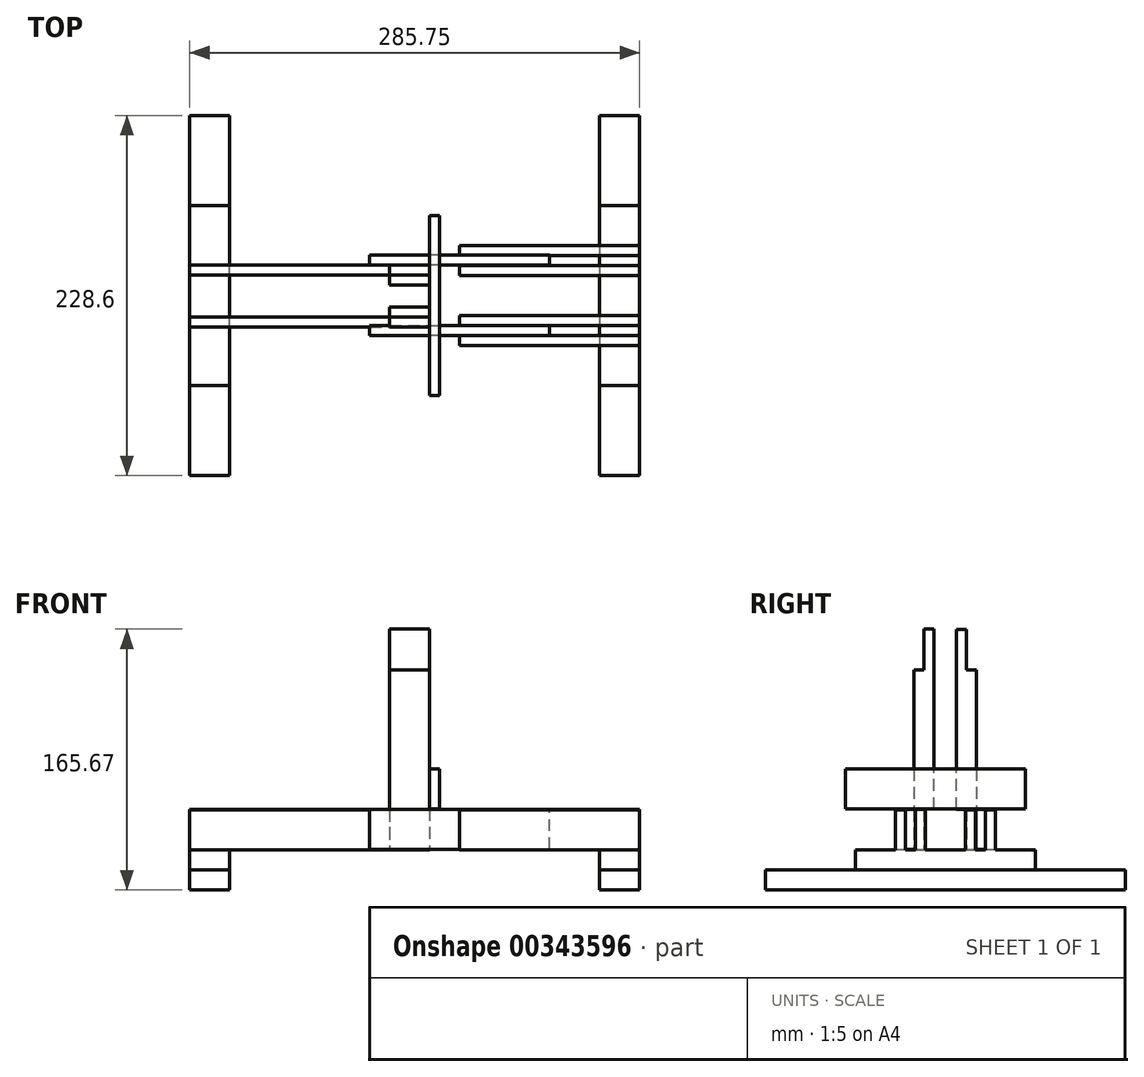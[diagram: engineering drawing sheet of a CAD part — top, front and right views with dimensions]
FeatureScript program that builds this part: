
annotation { "Feature Type Name" : "Feature", "Feature Type Description" : "" }
export const myFeature = defineFeature(function(context is Context, id is Id, definition is map)
    precondition{}
    {
        {
            var Q0;
            Q0=qCreatedBy(makeId("Top.planeOp"),FACE);
            var sketch = newSketch(context, id + "F0", { "sketchPlane" : qUnion([Q0])});
            skLineSegment(sketch, "E0.bottom", {"start": v(0, 0) * mm, "end": v(25.4, 0) * mm});
            skLineSegment(sketch, "E0.top", {"start": v(0, 114.3) * mm, "end": v(25.4, 114.3) * mm});
            skLineSegment(sketch, "E0.left", {"start": v(0, 0) * mm, "end": v(0, 114.3) * mm});
            skLineSegment(sketch, "E0.right", {"start": v(25.4, 0) * mm, "end": v(25.4, 114.3) * mm});
            skLineSegment(sketch, "E1.bottom", {"start": v(-234.95, 0) * mm, "end": v(-260.35, 0) * mm});
            skLineSegment(sketch, "E1.top", {"start": v(-234.95, 114.3) * mm, "end": v(-260.35, 114.3) * mm});
            skLineSegment(sketch, "E1.left", {"start": v(-234.95, 0) * mm, "end": v(-234.95, 114.3) * mm});
            skLineSegment(sketch, "E1.right", {"start": v(-260.35, 0) * mm, "end": v(-260.35, 114.3) * mm});
            skLineSegment(sketch, "E2.bottom", {"start": v(-260.35, 114.3) * mm, "end": v(-234.95, 114.3) * mm});
            skLineSegment(sketch, "E2.top", {"start": v(-260.35, 228.6) * mm, "end": v(-234.95, 228.6) * mm});
            skLineSegment(sketch, "E2.left", {"start": v(-260.35, 114.3) * mm, "end": v(-260.35, 228.6) * mm});
            skLineSegment(sketch, "E2.right", {"start": v(-234.95, 114.3) * mm, "end": v(-234.95, 228.6) * mm});
            skLineSegment(sketch, "E3.top", {"start": v(0, 228.6) * mm, "end": v(25.4, 228.6) * mm});
            skLineSegment(sketch, "E3.left", {"start": v(0, 114.3) * mm, "end": v(0, 228.6) * mm});
            skLineSegment(sketch, "E3.right", {"start": v(25.4, 114.3) * mm, "end": v(25.4, 228.6) * mm});
            skSolve(sketch);
        }
        {
            var Q0;
            Q0 = qSketchRegion(id + "F0", true);
            extrude(context, id + "F1", {"entities" : qUnion([Q0]), "depth" : 12.7 * mm});
        }
        {
            var Q0;
            Q0=makeQuery(id+"F1.opExtrude","CAP_FACE",FACE,{"disambiguationData":[OSD([sQuery(id+"F0.wireOp",EDGE,"E1.bottom"),sQuery(id+"F0.wireOp",EDGE,"E1.left"),sQuery(id+"F0.wireOp",EDGE,"E1.right"),sQuery(id+"F0.wireOp",EDGE,"E2.top"),sQuery(id+"F0.wireOp",EDGE,"E2.left"),sQuery(id+"F0.wireOp",EDGE,"E2.right")])],"isStart":false});
            var sketch = newSketch(context, id + "F2", { "sketchPlane" : qUnion([Q0])});
            skLineSegment(sketch, "E4.bottom", {"start": v(-260.35, 57.15) * mm, "end": v(-234.95, 57.15) * mm});
            skLineSegment(sketch, "E4.top", {"start": v(-260.35, 171.45) * mm, "end": v(-234.95, 171.45) * mm});
            skLineSegment(sketch, "E4.left", {"start": v(-260.35, 57.15) * mm, "end": v(-260.35, 171.45) * mm});
            skLineSegment(sketch, "E4.right", {"start": v(-234.95, 57.15) * mm, "end": v(-234.95, 171.45) * mm});
            skLineSegment(sketch, "E5.bottom", {"start": v(0, 171.45) * mm, "end": v(25.4, 171.45) * mm});
            skLineSegment(sketch, "E5.top", {"start": v(0, 57.15) * mm, "end": v(25.4, 57.15) * mm});
            skLineSegment(sketch, "E5.left", {"start": v(0, 171.45) * mm, "end": v(0, 57.15) * mm});
            skLineSegment(sketch, "E5.right", {"start": v(25.4, 171.45) * mm, "end": v(25.4, 57.15) * mm});
            skSolve(sketch);
        }
        {
            var Q0;
            Q0 = qSketchRegion(id + "F2", true);
            extrude(context, id + "F3", {"entities" : qUnion([Q0]), "depth" : 12.7 * mm});
        }
        {
            var Q0;
            Q0=makeQuery(id+"F3.opExtrude","SWEPT_FACE",FACE,{"disambiguationData":[OSD([sQuery(id+"F2.wireOp",EDGE,"E5.right")])]});
            var sketch = newSketch(context, id + "F4", { "sketchPlane" : qUnion([Q0])});
            skLineSegment(sketch, "E6.bottom", {"start": v(82.55, 25.4) * mm, "end": v(88.9, 25.4) * mm});
            skLineSegment(sketch, "E6.top", {"start": v(82.55, 50.8) * mm, "end": v(88.9, 50.8) * mm});
            skLineSegment(sketch, "E6.left", {"start": v(82.55, 25.4) * mm, "end": v(82.55, 50.8) * mm});
            skLineSegment(sketch, "E6.right", {"start": v(88.9, 25.4) * mm, "end": v(88.9, 50.8) * mm});
            skLineSegment(sketch, "E7.bottom", {"start": v(139.7, 25.4) * mm, "end": v(146.05, 25.4) * mm});
            skLineSegment(sketch, "E7.top", {"start": v(139.7, 50.8) * mm, "end": v(146.05, 50.8) * mm});
            skLineSegment(sketch, "E7.left", {"start": v(139.7, 25.4) * mm, "end": v(139.7, 50.8) * mm});
            skLineSegment(sketch, "E7.right", {"start": v(146.05, 25.4) * mm, "end": v(146.05, 50.8) * mm});
            skLineSegment(sketch, "E8.bottom", {"start": v(95.25, 25.4) * mm, "end": v(101.6, 25.4) * mm});
            skLineSegment(sketch, "E8.top", {"start": v(95.25, 51.24) * mm, "end": v(101.6, 51.24) * mm});
            skLineSegment(sketch, "E8.left", {"start": v(95.25, 25.4) * mm, "end": v(95.25, 51.24) * mm});
            skLineSegment(sketch, "E8.right", {"start": v(101.6, 25.4) * mm, "end": v(101.6, 51.24) * mm});
            skLineSegment(sketch, "E9.bottom", {"start": v(127, 25.4) * mm, "end": v(133.35, 25.4) * mm});
            skLineSegment(sketch, "E9.top", {"start": v(127, 50.9) * mm, "end": v(133.35, 50.9) * mm});
            skLineSegment(sketch, "E9.left", {"start": v(127, 25.4) * mm, "end": v(127, 50.9) * mm});
            skLineSegment(sketch, "E9.right", {"start": v(133.35, 25.4) * mm, "end": v(133.35, 50.9) * mm});
            skSolve(sketch);
        }
        {
            var Q0;
            Q0 = qSketchRegion(id + "F4", true);
            extrude(context, id + "F5", {"entities" : qUnion([Q0]), "operationType" : NewBodyOperationType.ADD, "oppositeDirection" : true, "depth" : 114.3 * mm});
        }
        {
            var Q0;
            Q0=makeQuery(id+"F5.opExtrude","SWEPT_FACE",FACE,{"disambiguationData":[OSD([sQuery(id+"F4.wireOp",EDGE,"E8.top")])]});
            var sketch = newSketch(context, id + "F6", { "sketchPlane" : qUnion([Q0])});
            skLineSegment(sketch, "E10.bottom", {"start": v(-31.75, 95.25) * mm, "end": v(-146.05, 95.25) * mm});
            skLineSegment(sketch, "E10.top", {"start": v(-31.75, 88.9) * mm, "end": v(-146.05, 88.9) * mm});
            skLineSegment(sketch, "E10.left", {"start": v(-31.75, 95.25) * mm, "end": v(-31.75, 88.9) * mm});
            skLineSegment(sketch, "E10.right", {"start": v(-146.05, 95.25) * mm, "end": v(-146.05, 88.9) * mm});
            skPoint(sketch, "E11.firstSnap0", {"position": v(-31.75, 101.6) * mm});
            skLineSegment(sketch, "E11.bottom", {"start": v(-31.75, 140.03) * mm, "end": v(-146.05, 140.03) * mm});
            skLineSegment(sketch, "E11.top", {"start": v(-31.75, 133.68) * mm, "end": v(-146.05, 133.68) * mm});
            skLineSegment(sketch, "E11.left", {"start": v(-31.75, 140.03) * mm, "end": v(-31.75, 133.68) * mm});
            skLineSegment(sketch, "E11.right", {"start": v(-146.05, 140.03) * mm, "end": v(-146.05, 133.68) * mm});
            skSolve(sketch);
        }
        {
            var Q0;
            Q0 = qSketchRegion(id + "F6", true);
            extrude(context, id + "F7", {"entities" : qUnion([Q0]), "oppositeDirection" : true, "depth" : 25.4 * mm});
        }
        {
            var Q0;
            Q0=makeQuery(id+"F7.opExtrude","SWEPT_FACE",FACE,{"disambiguationData":[OSD([sQuery(id+"F6.wireOp",EDGE,"E11.top")])]});
            var sketch = newSketch(context, id + "F8", { "sketchPlane" : qUnion([Q0])});
            skLineSegment(sketch, "E12.bottom", {"start": v(-133.35, 51.24) * mm, "end": v(-260.35, 51.24) * mm});
            skLineSegment(sketch, "E12.top", {"start": v(-133.35, 25.84) * mm, "end": v(-260.35, 25.84) * mm});
            skLineSegment(sketch, "E12.left", {"start": v(-133.35, 51.24) * mm, "end": v(-133.35, 25.84) * mm});
            skLineSegment(sketch, "E12.right", {"start": v(-260.35, 51.24) * mm, "end": v(-260.35, 25.84) * mm});
            skSolve(sketch);
        }
        {
            var Q0;
            Q0=makeQuery(id+"F8.imprint","IMPRINT",FACE,{"disambiguationData":[TD([[makeQuery(id+"F8.imprint","IMPRINT",EDGE,{"derivedFrom":sQuery(id+"F8.wireOp",EDGE,"E12.bottom")}),1.0]])]});
            extrude(context, id + "F9", {"entities" : qUnion([Q0]), "depth" : 6.35 * mm});
        }
        {
            var Q0;
            Q0=makeQuery(id+"F3.opExtrude","CAP_FACE",FACE,{"disambiguationData":[OSD([sQuery(id+"F2.wireOp",EDGE,"E4.bottom"),sQuery(id+"F2.wireOp",EDGE,"E4.top"),sQuery(id+"F2.wireOp",EDGE,"E4.left"),sQuery(id+"F2.wireOp",EDGE,"E4.right")])],"isStart":false});
            var sketch = newSketch(context, id + "F10", { "sketchPlane" : qUnion([Q0])});
            skLineSegment(sketch, "E13.bottom", {"start": v(-260.35, 94.23) * mm, "end": v(-133.35, 94.23) * mm});
            skLineSegment(sketch, "E13.top", {"start": v(-260.35, 100.58) * mm, "end": v(-133.35, 100.58) * mm});
            skLineSegment(sketch, "E13.left", {"start": v(-260.35, 94.23) * mm, "end": v(-260.35, 100.58) * mm});
            skLineSegment(sketch, "E13.right", {"start": v(-133.35, 94.23) * mm, "end": v(-133.35, 100.58) * mm});
            skSolve(sketch);
        }
        {
            var Q0;
            Q0 = qSketchRegion(id + "F10", true);
            extrude(context, id + "F11", {"entities" : qUnion([Q0]), "depth" : 25.4 * mm});
        }
        {
            var Q0;
            Q0=makeQuery(id+"F11.opExtrude","CAP_FACE",FACE,{"disambiguationData":[OSD([sQuery(id+"F10.wireOp",EDGE,"E13.bottom"),sQuery(id+"F10.wireOp",EDGE,"E13.top"),sQuery(id+"F10.wireOp",EDGE,"E13.left"),sQuery(id+"F10.wireOp",EDGE,"E13.right")])],"isStart":true});
            var sketch = newSketch(context, id + "F12", { "sketchPlane" : qUnion([Q0])});
            skPoint(sketch, "E14.left.start.orphan", {"position": v(-88.9, -133.2) * mm});
            skLineSegment(sketch, "E15.bottom", {"start": v(-133.35, -94.23) * mm, "end": v(-107.95, -94.23) * mm});
            skLineSegment(sketch, "E15.top", {"start": v(-133.35, -100.58) * mm, "end": v(-107.95, -100.58) * mm});
            skLineSegment(sketch, "E15.left", {"start": v(-133.35, -94.23) * mm, "end": v(-133.35, -100.58) * mm});
            skLineSegment(sketch, "E15.right", {"start": v(-107.95, -94.23) * mm, "end": v(-107.95, -100.58) * mm});
            skLineSegment(sketch, "E16.bottom", {"start": v(-133.35, -127.38) * mm, "end": v(-107.95, -127.38) * mm});
            skLineSegment(sketch, "E16.top", {"start": v(-133.35, -133.73) * mm, "end": v(-107.95, -133.73) * mm});
            skLineSegment(sketch, "E16.left", {"start": v(-133.35, -127.38) * mm, "end": v(-133.35, -133.73) * mm});
            skLineSegment(sketch, "E16.right", {"start": v(-107.95, -127.38) * mm, "end": v(-107.95, -133.73) * mm});
            skSolve(sketch);
        }
        {
            var Q0;
            Q0 = qSketchRegion(id + "F12", true);
            extrude(context, id + "F13", {"entities" : qUnion([Q0]), "oppositeDirection" : true, "depth" : 114.3 * mm});
        }
        {
            var Q0;
            Q0=makeQuery(id+"F13.opExtrude","SWEPT_FACE",FACE,{"disambiguationData":[OSD([sQuery(id+"F12.wireOp",EDGE,"E16.right")])]});
            var sketch = newSketch(context, id + "F14", { "sketchPlane" : qUnion([Q0])});
            skLineSegment(sketch, "E17.bottom", {"start": v(127.38, 51.22) * mm, "end": v(121.03, 51.22) * mm});
            skLineSegment(sketch, "E17.top", {"start": v(127.38, 165.52) * mm, "end": v(121.03, 165.52) * mm});
            skLineSegment(sketch, "E17.left", {"start": v(127.38, 51.22) * mm, "end": v(127.38, 165.52) * mm});
            skLineSegment(sketch, "E17.right", {"start": v(121.03, 51.22) * mm, "end": v(121.03, 165.52) * mm});
            skSolve(sketch);
        }
        {
            var Q0;
            Q0 = qSketchRegion(id + "F14", true);
            extrude(context, id + "F15", {"entities" : qUnion([Q0]), "oppositeDirection" : true, "depth" : 25.4 * mm});
        }
        {
            var Q0;
            Q0=makeQuery(id+"F13.opExtrude","SWEPT_FACE",FACE,{"disambiguationData":[OSD([sQuery(id+"F12.wireOp",EDGE,"E15.right")])]});
            var sketch = newSketch(context, id + "F16", { "sketchPlane" : qUnion([Q0])});
            skLineSegment(sketch, "E18.bottom", {"start": v(100.58, 51.37) * mm, "end": v(106.93, 51.37) * mm});
            skLineSegment(sketch, "E18.top", {"start": v(100.58, 165.67) * mm, "end": v(106.93, 165.67) * mm});
            skLineSegment(sketch, "E18.left", {"start": v(100.58, 51.37) * mm, "end": v(100.58, 165.67) * mm});
            skLineSegment(sketch, "E18.right", {"start": v(106.93, 51.37) * mm, "end": v(106.93, 165.67) * mm});
            skSolve(sketch);
        }
        {
            var Q0;
            Q0 = qSketchRegion(id + "F16", true);
            extrude(context, id + "F17", {"entities" : qUnion([Q0]), "oppositeDirection" : true, "depth" : 25.4 * mm});
        }
        {
            var Q0;
            Q0=makeQuery(id+"F17.opExtrude","CAP_FACE",FACE,{"disambiguationData":[OSD([sQuery(id+"F16.wireOp",EDGE,"E18.bottom"),sQuery(id+"F16.wireOp",EDGE,"E18.top"),sQuery(id+"F16.wireOp",EDGE,"E18.left"),sQuery(id+"F16.wireOp",EDGE,"E18.right")])],"isStart":true});
            var sketch = newSketch(context, id + "F18", { "sketchPlane" : qUnion([Q0])});
            skLineSegment(sketch, "E19.bottom", {"start": v(50.8, 51.37) * mm, "end": v(165.1, 51.37) * mm});
            skLineSegment(sketch, "E19.top", {"start": v(50.8, 76.77) * mm, "end": v(165.1, 76.77) * mm});
            skLineSegment(sketch, "E19.left", {"start": v(50.8, 51.37) * mm, "end": v(50.8, 76.77) * mm});
            skLineSegment(sketch, "E19.right", {"start": v(165.1, 51.37) * mm, "end": v(165.1, 76.77) * mm});
            skSolve(sketch);
        }
        {
            var Q0;
            Q0 = qSketchRegion(id + "F18", true);
            extrude(context, id + "F19", {"entities" : qUnion([Q0]), "operationType" : NewBodyOperationType.ADD, "depth" : 6.35 * mm});
        }
    });
